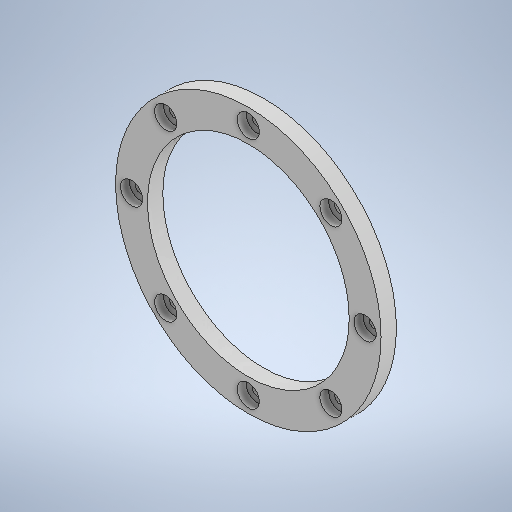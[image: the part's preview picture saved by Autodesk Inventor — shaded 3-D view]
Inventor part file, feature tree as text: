
AUTODESK INVENTOR PART (.ipt)
format: ipt  version: 2025 (Build 290162010, 162A)  size: 396,288 bytes
history: native  units: mm
features: extrude x5, sketch x5, projected_geometry x3, pattern_circular x1, other x1
ambient origin geometry x8: Origin, YZ Plane, XZ Plane, XY Plane, X Axis, Y Axis, Z Axis, Center Point
bodies: Solid1 (feature_tree)
feature tree (15):
  extrude  "Extrusion1"  Depth=250.0mm
  extrude  "Extrusion2"  Depth=41.0mm
  extrude  "Extrusion3"  Depth=80.0mm TaperAngle=360.0deg
  pattern_circular  "Circular Pattern1"  [2 undecoded]
  extrude  "Extrusion4"  Depth=10.0mm TaperAngle=0.0deg
  extrude  "Extrusion5"  Depth=10.0mm
  sketch  "Sketch1"  dims[d0=39.5mm d1=250.0mm]
  sketch  "Sketch2"  dims[d2=41.0mm d3=0.0mm d4=12.5mm]
  projected_geometry  "Projected Loop1"
  sketch  "Sketch3"  dims[d5=0.0mm d6=0.0mm d7=80.0mm d8=360.0deg]
  sketch  "Sketch4"  dims[d10=27.5mm]
  sketch  "Sketch5"  dims[d11=11.0mm d12=0.0mm d13=5.0mm d14=10.0mm d15=0.0mm d17=22.0mm d18=0.0mm d19=0.0mm]
  projected_geometry  "Projected Loop2"
  projected_geometry  "Projected Loop3"
  other  "Definition1"
note: 2 required parameter values undecoded (feature->parameter linkage not recoverable at this tier; creation-order binding heuristic only, values carry confidence <= 0.55)
